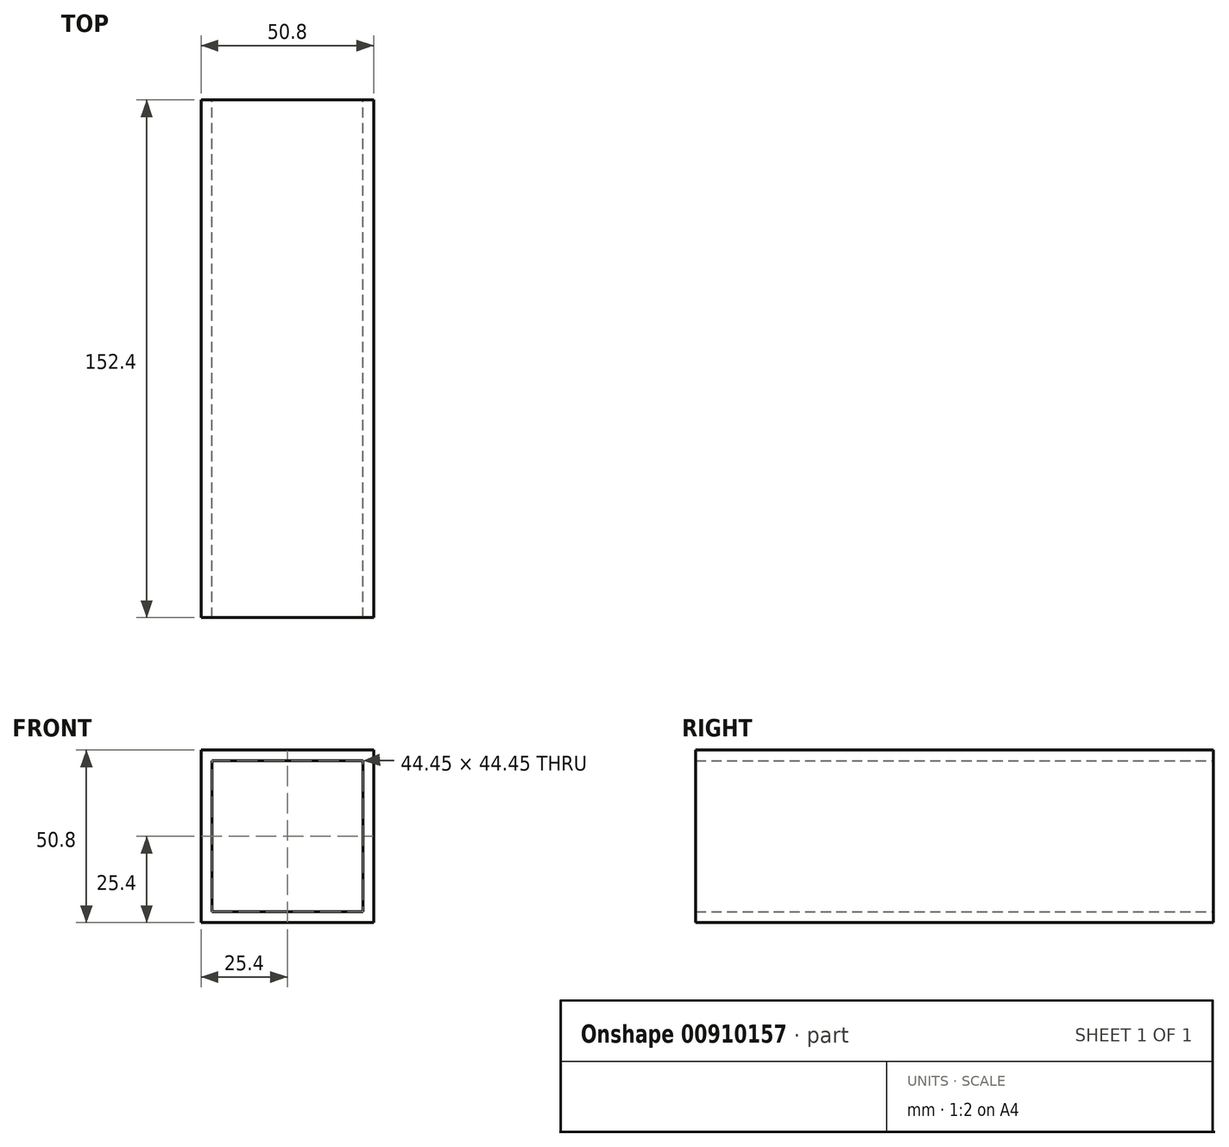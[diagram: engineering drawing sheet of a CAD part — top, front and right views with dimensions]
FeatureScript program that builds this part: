
annotation { "Feature Type Name" : "Feature", "Feature Type Description" : "" }
export const myFeature = defineFeature(function(context is Context, id is Id, definition is map)
    precondition{}
    {
        {
            var Q0;
            Q0=qCreatedBy(makeId("Front.planeOp"),FACE);
            var sketch = newSketch(context, id + "F0", { "sketchPlane" : qUnion([Q0])});
            skLineSegment(sketch, "E0.bottom", {"start": v(-25.4, 25.4) * mm, "end": v(25.4, 25.4) * mm});
            skLineSegment(sketch, "E0.top", {"start": v(-25.4, -25.4) * mm, "end": v(25.4, -25.4) * mm});
            skLineSegment(sketch, "E0.left", {"start": v(-25.4, 25.4) * mm, "end": v(-25.4, -25.4) * mm});
            skLineSegment(sketch, "E0.right", {"start": v(25.4, 25.4) * mm, "end": v(25.4, -25.4) * mm});
            skPoint(sketch, "E0.middle", {"position": v(0, 0) * mm});
            skSolve(sketch);
        }
        {
            var Q0;
            Q0 = qSketchRegion(id + "F0", true);
            extrude(context, id + "F1", {"entities" : qUnion([Q0]), "endBound" : BoundingType.SYMMETRIC, "depth" : 152.4 * mm, "offsetDistance" : 25.4 * mm});
        }
        {
            var Q0;
            Q0=makeQuery(id+"F1.opExtrude","CAP_FACE",FACE,{"disambiguationData":[OSD([sQuery(id+"F0.wireOp",EDGE,"E0.bottom"),sQuery(id+"F0.wireOp",EDGE,"E0.top"),sQuery(id+"F0.wireOp",EDGE,"E0.left"),sQuery(id+"F0.wireOp",EDGE,"E0.right")])],"isStart":true});
            var Q1;
            Q1=makeQuery(id+"F1.opExtrude","CAP_FACE",FACE,{"disambiguationData":[OSD([sQuery(id+"F0.wireOp",EDGE,"E0.bottom"),sQuery(id+"F0.wireOp",EDGE,"E0.top"),sQuery(id+"F0.wireOp",EDGE,"E0.left"),sQuery(id+"F0.wireOp",EDGE,"E0.right")])],"isStart":false});
            shell(context, id + "F2", {"entities" : qUnion([Q0, Q1]), "thickness" : 3.17 * mm});
        }
    });
